# Revit family: Gira_530100
name_source: partatom
category: Electrical Fixtures
revit_build: Autodesk Revit 2017 (Build: 20160225_1515(x64)
units: mm (PartAtom-declared; Revit-internal decimal feet)

## family parameters
Cut with Voids When Loaded = No
Host = Face
Maintain Annotation Orientation = No
Part Type = Normal
Room Calculation Point = No
Round Connector Dimension = Use Diameter
Shared = No

## types (1)
- Server DRA Gira eNet
    BIM = https://media.live.bim.site 00_REG 6.rfa
    BIMSITE_PRODUCT_ID = 34688062b31a76825875535aa20c87b21f15bcc9
    Cost = 0 $
    Default Elevation = 1219 mm
    Description = Server DRA eNet eNet Server,DRA Features: - Operation with eNet SMART HOME app for Apple iOS or Android or with Gira G1. - Visualisation of the Gira interface via Gira Control 9 Client. - Fully encrypted wireless transmission (AES CCM 128-bit) from eNet Server software version 2.0. - Compatible with smart heating control of tado as of eNet Server software version 2.1 - Wireless transmitter and wireless receiver for max. 32 eNet wireless DIN-rail mounting devices (eNet wireless receiver module DRA is not required). - Internal eNet wireless and WLAN antenna. - External eNet wireless and WLAN antennas can be connected. - Functions: Switching or pressing, dimming, blind. - Energy management, scenes, connections, timers, if-then rules - Updates and configures eNet SMART HOME devices. - Integrated telegram recording for diagnostics. - Automatically generated project documentation. - Optional remote access via My-eNet portal is compatible to IPv4 and IPv6.,Notes : - The eNet server should be installed at a central location, where possible (e.g. ground floor) in order to guarantee good reception quality. - Installation in a distribution box or sub-distribution with a metal housing requires an additional antenna. The additional antenna is to be placed outside the metal housing. - The server is started up using the eNet SMART HOME connect web interface. To start up the server via the web interface, the start-up computer must have a current browser (e.g. Mozilla Firefox, Microsoft Internet Explorer, Edge, Safari, or Chrome). - The power supply is required for power supply when installed. - Installation on top-hat rail. - Not compatible with the Gira wireless bus system.
    GTIN = 4010337591306
    HAN = 530100
    HeinzeBIM = https://www.heinze.de
    Manufacturer = Gira
    URL = https://www.gira.de

## geometry (parser evidence)
native form markers: Blend x2, Sweep x3
no freeform markers — native parametric forms only
